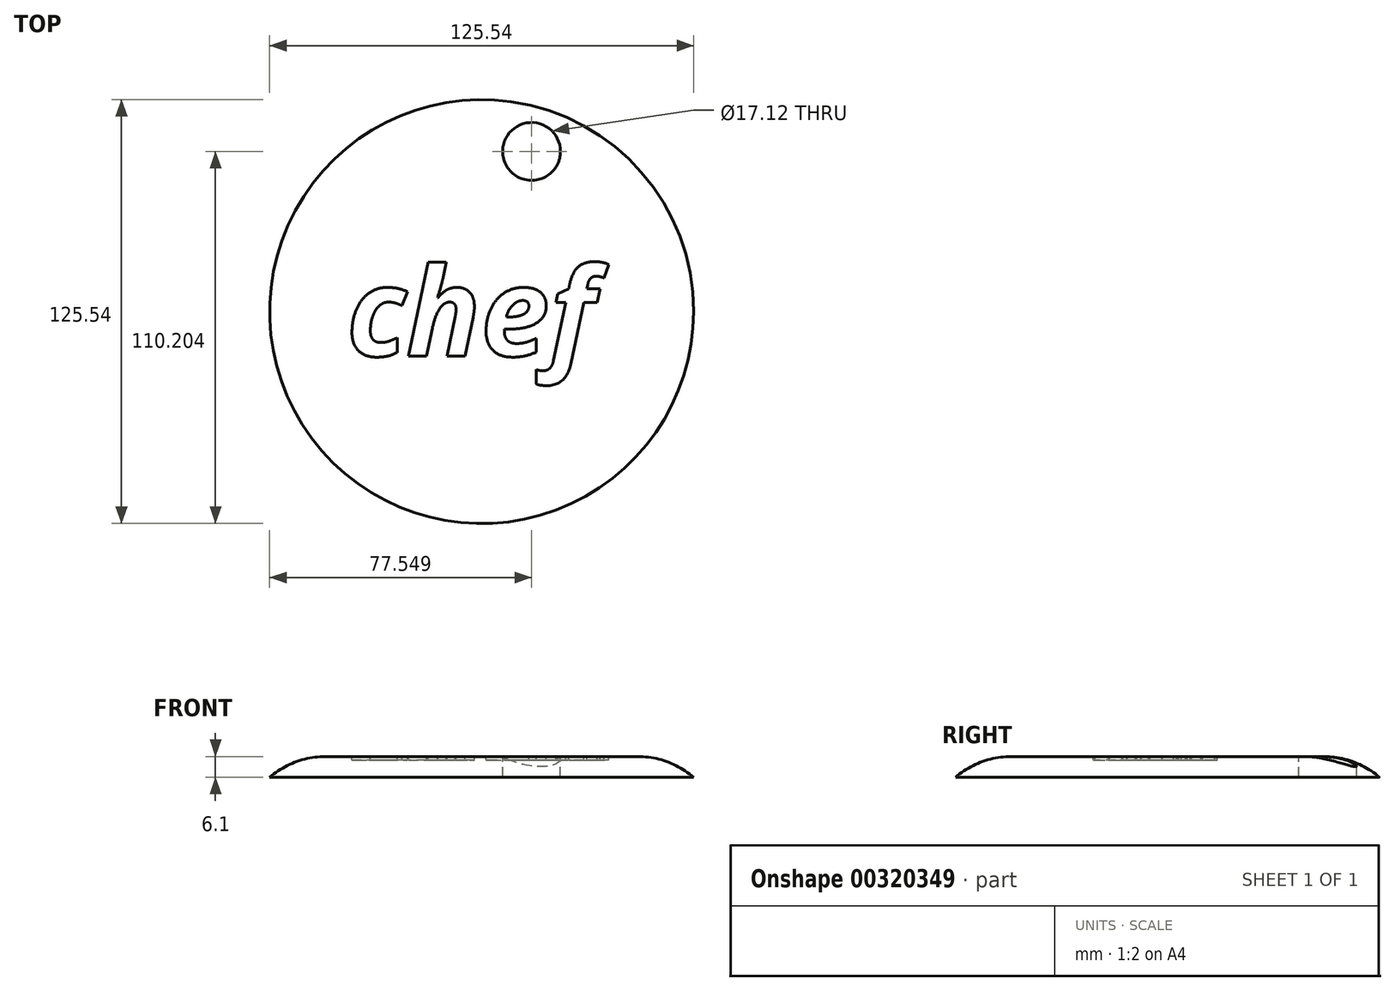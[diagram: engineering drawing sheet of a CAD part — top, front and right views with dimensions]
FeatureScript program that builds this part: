
annotation { "Feature Type Name" : "Feature", "Feature Type Description" : "" }
export const myFeature = defineFeature(function(context is Context, id is Id, definition is map)
    precondition{}
    {
        {
            var Q0;
            Q0=qCreatedBy(makeId("Top.planeOp"),FACE);
            var sketch = newSketch(context, id + "F0", { "sketchPlane" : qUnion([Q0])});
            skCircle(sketch, "E0", {"center": v(0, 0) * mm, "radius": 62.77 * mm});
            skSolve(sketch);
        }
        {
            var Q0;
            Q0=makeQuery(id+"F0.imprint","IMPRINT",FACE,{"disambiguationData":[TD([[makeQuery(id+"F0.imprint","IMPRINT",EDGE,{"derivedFrom":sQuery(id+"F0.wireOp",EDGE,"E0")}),1.0]])]});
            extrude(context, id + "F1", {"entities" : qUnion([Q0]), "depth" : 6.1 * mm});
        }
        {
            var Q0;
            Q0=makeQuery(id+"F1.opExtrude","CAP_FACE",FACE,{"disambiguationData":[OSD([sQuery(id+"F0.wireOp",EDGE,"E0")])],"isStart":false});
            var sketch = newSketch(context, id + "F2", { "sketchPlane" : qUnion([Q0])});
            skCircle(sketch, "E1", {"center": v(14.78, 47.43) * mm, "radius": 8.56 * mm});
            skSolve(sketch);
        }
        {
            var Q0;
            Q0=sQuery(id+"F2.wireOp",EDGE,"E1");
            extrude(context, id + "F3", {"bodyType" : ToolBodyType.SURFACE, "surfaceEntities" : qUnion([Q0]), "endBound" : BoundingType.THROUGH_ALL, "oppositeDirection" : true, "depth" : 283.6 * mm});
        }
        {
            var Q0;
            Q0=makeQuery(id+"F3.opExtrude","SWEPT_BODY",BODY,{"disambiguationData":[OSD([sQuery(id+"F2.wireOp",EDGE,"E1")])]});
            deleteBodies(context, id + "F4", {"entities" : qUnion([Q0])});
        }
        {
            var Q0;
            Q0=makeQuery(id+"F2.imprint","IMPRINT",FACE,{"disambiguationData":[TD([[makeQuery(id+"F2.imprint","IMPRINT",EDGE,{"derivedFrom":sQuery(id+"F2.wireOp",EDGE,"E1")}),1.0]])]});
            extrude(context, id + "F5", {"entities" : qUnion([Q0]), "operationType" : NewBodyOperationType.REMOVE, "endBound" : BoundingType.THROUGH_ALL, "oppositeDirection" : true, "depth" : 25.4 * mm});
        }
        {
            var Q0;
            Q0=makeQuery(id+"F1.opExtrude","CAP_EDGE",EDGE,{"disambiguationData":[OSD([sQuery(id+"F0.wireOp",EDGE,"E0")])],"isStart":false});
            fillet(context, id + "F6", {"entities" : qUnion([Q0]), "radius" : 25.4 * mm, "tangentPropagation" : true, "allowEdgeOverflow" : false});
        }
        {
            var Q0;
            Q0=makeQuery(id+"F1.opExtrude","CAP_FACE",FACE,{"disambiguationData":[OSD([sQuery(id+"F0.wireOp",EDGE,"E0")])],"isStart":false});
            var sketch = newSketch(context, id + "F7", { "sketchPlane" : qUnion([Q0])});
            skText(sketch, "E2", { "text": "chef", "fontName": "OpenSans-BoldItalic.ttf"});
            const initialGuessF7  = {"E2": [-0.04, -0.01315, 1, 0, 0.0263]};
            skSetInitialGuess(sketch, initialGuessF7);
            skSolve(sketch);
        }
        {
            var Q0;
            Q0 = qSketchRegion(id + "F7", true);
            extrude(context, id + "F8", {"entities" : qUnion([Q0]), "operationType" : NewBodyOperationType.REMOVE, "oppositeDirection" : true, "depth" : 1 * mm});
        }
    });
